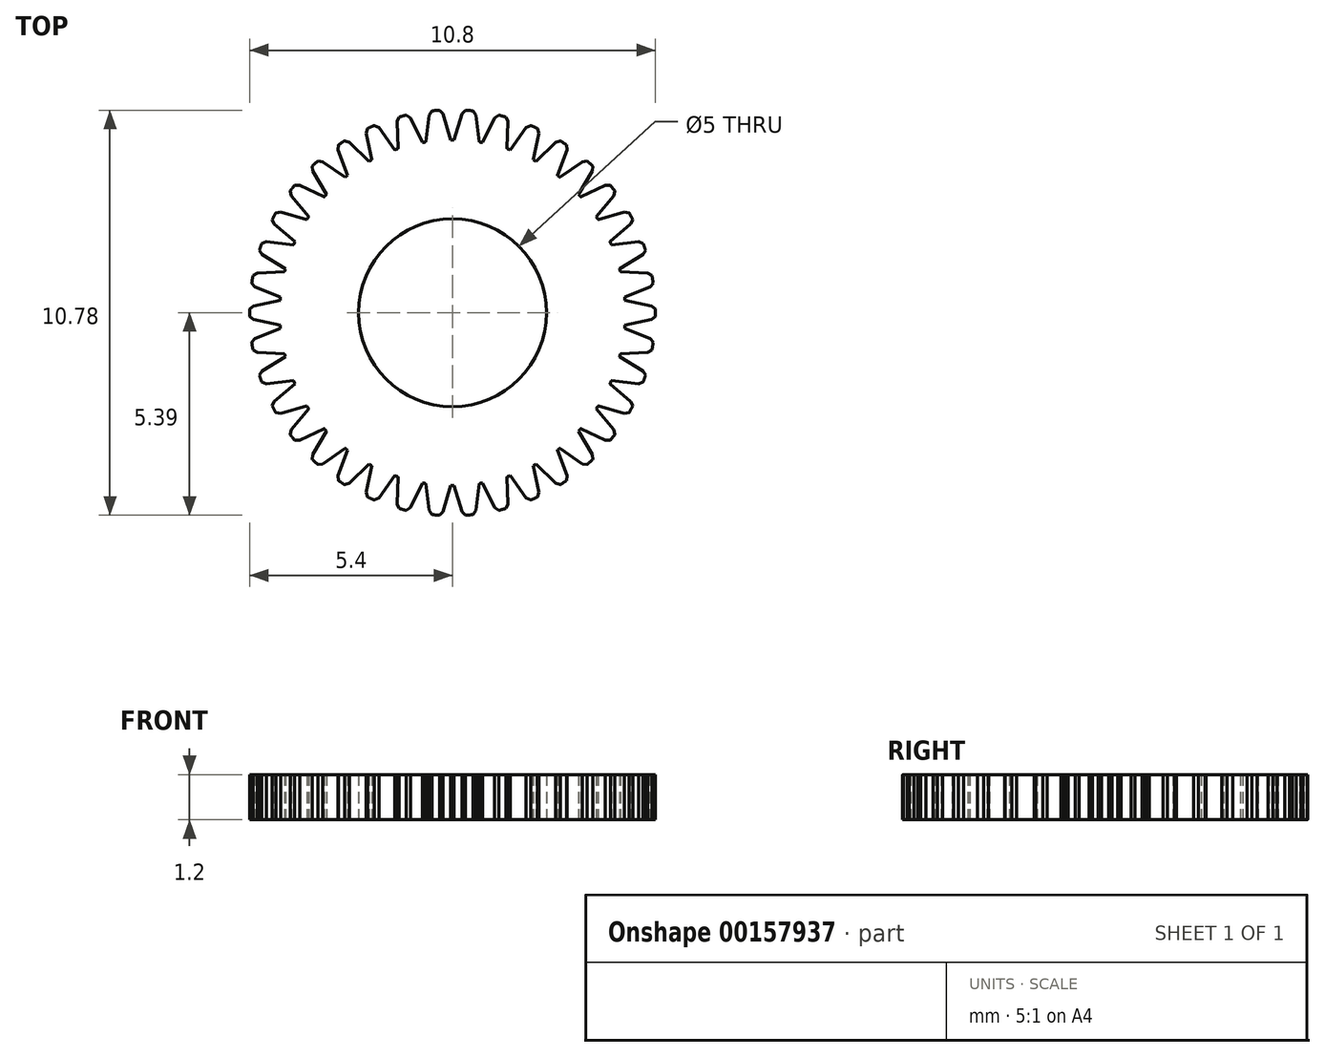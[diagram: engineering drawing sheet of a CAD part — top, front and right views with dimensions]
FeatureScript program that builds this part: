
annotation { "Feature Type Name" : "Feature", "Feature Type Description" : "" }
export const myFeature = defineFeature(function(context is Context, id is Id, definition is map)
    precondition{}
    {
        {
            assignVariable(context, id + "F0", {"name" : "D", "anyValue" : 1.08});
        }
        {
            assignVariable(context, id + "F1", {"name" : "n", "anyValue" : 38});
        }
        {
            assignVariable(context, id + "F2", {"name" : "h", "anyValue" : 1.2});
        }
        {
            var Q0;
            Q0=qCreatedBy(makeId("Front.planeOp"),FACE);
            var sketch = newSketch(context, id + "F3", { "sketchPlane" : qUnion([Q0])});
            skLineSegment(sketch, "E0", {"start": v(0, 0) * mm, "end": v(0, 36.61) * mm, "construction": true});
            skSolve(sketch);
        }
        {
            var Q0;
            Q0=qCreatedBy(makeId("Top.planeOp"),FACE);
            var sketch = newSketch(context, id + "F4", { "sketchPlane" : qUnion([Q0])});
            skCircle(sketch, "E1", {"center": v(0, 0) * mm, "radius": 5.4 * mm});
            skCircle(sketch, "E2", {"center": v(0, 0) * mm, "radius": 2.5 * mm});
            skCircle(sketch, "E3", {"center": v(0, 0) * mm, "radius": 4.6 * mm});
            skLineSegment(sketch, "E4", {"start": v(0, 0) * mm, "end": v(0, 5.4) * mm});
            skLineSegment(sketch, "E5", {"start": v(0, 0) * mm, "end": v(0.89, 5.33) * mm});
            skLineSegment(sketch, "E6", {"start": v(0, 0) * mm, "end": v(0.45, 5.38) * mm, "construction": true});
            skCircle(sketch, "E7", {"center": v(0, 0) * mm, "radius": 5 * mm, "construction": true});
            skLineSegment(sketch, "E8", {"start": v(0.28, 5.4) * mm, "end": v(0.04, 4.6) * mm});
            skLineSegment(sketch, "E9.MirrorCS", {"start": v(0.6, 5.37) * mm, "end": v(0.71, 4.54) * mm});
            skLineSegment(sketch, "E10", {"start": v(0.18, 5.4) * mm, "end": v(0, 0) * mm, "construction": true});
            skPoint(sketch, "E11", {"position": v(0.16, 5) * mm});
            skLineSegment(sketch, "E12", {"start": v(0.35, 5.39) * mm, "end": v(0.25, 5.3) * mm});
            skLineSegment(sketch, "E13.MirrorCS", {"start": v(0.54, 5.37) * mm, "end": v(0.62, 5.26) * mm});
            skSolve(sketch);
        }
        {
            var Q0;
            {var subQ6=sQuery(id+"F4.wireOp",EDGE,"E12");Q0=makeQuery(id+"F4.imprint","IMPRINT",FACE,{"disambiguationData":[TD([[makeQuery(id+"F4.imprint","IMPRINT",EDGE,{"derivedFrom":subQ6}),1.0]])]});}
            var Q1;
            {var subQ2=sQuery(id+"F4.wireOp",EDGE,"E4");var subQ7=sQuery(id+"F4.wireOp",EDGE,"E2");var subQ8=makeQuery(id+"F4.imprint","INTERSECT",VERTEX,{"derivedFrom":[subQ7,subQ2]});Q1=makeQuery(id+"F4.imprint","IMPRINT",FACE,{"disambiguationData":[TD([[makeQuery(id+"F4.imprint","IMPRINT",EDGE,{"disambiguationData":[TD([[subQ8,1.0]])],"derivedFrom":subQ7}),-1.0]])]});}
            extrude(context, id + "F5", {"entities" : qUnion([Q0, Q1]), "endBound" : BoundingType.SYMMETRIC, "depth" : (getVariable(context, 'h')) * mm});
        }
        {
            var Q0;
            Q0=makeQuery(id+"F5.opExtrude","SWEPT_BODY",BODY,{"disambiguationData":[OSD([sQuery(id+"F4.wireOp",EDGE,"E1"),sQuery(id+"F4.wireOp",EDGE,"E2"),sQuery(id+"F4.wireOp",EDGE,"E3"),sQuery(id+"F4.wireOp",EDGE,"E4"),sQuery(id+"F4.wireOp",EDGE,"E5"),sQuery(id+"F4.wireOp",EDGE,"E8"),sQuery(id+"F4.wireOp",EDGE,"E9.MirrorCS")])]});
            var Q1;
            Q1=sQuery(id+"F3.wireOp",EDGE,"E0");
            circularPattern(context, id + "F6", {"operationType" : NewBodyOperationType.ADD, "entities" : qUnion([Q0]), "axis" : qUnion([Q1]), "angle" : 360 * degree, "instanceCount" : getVariable(context, 'n'), "equalSpace" : true});
        }
        {
            var Q0;
            Q0=qCreatedBy(makeId("Front.planeOp"),FACE);
            cPlane(context, id + "F7", {"entities" : qUnion([Q0]), "cplaneType" : CPlaneType.OFFSET, "offset" : (getVariable(context, 'D') / 2) * mm, "width" : 150 * mm, "height" : 150 * mm});
        }
        {
            var Q0;
            Q0=qCreatedBy(id+"F7.planeOp",FACE);
            var sketch = newSketch(context, id + "F8", { "sketchPlane" : qUnion([Q0])});
            skLineSegment(sketch, "E14.bottom", {"start": v(5.4, 6) * mm, "end": v(-5.4, 6) * mm});
            skLineSegment(sketch, "E14.top", {"start": v(5.4, -6) * mm, "end": v(-5.4, -6) * mm});
            skLineSegment(sketch, "E14.left", {"start": v(5.4, 6) * mm, "end": v(5.4, -6) * mm});
            skLineSegment(sketch, "E14.right", {"start": v(-5.4, 6) * mm, "end": v(-5.4, -6) * mm});
            skPoint(sketch, "E14.middle", {"position": v(0, 0) * mm});
            skCircle(sketch, "E15", {"center": v(0, -4) * mm, "radius": 1.25 * mm});
            skSolve(sketch);
        }
        {
            var Q0;
            Q0=makeQuery(id+"F8.imprint","IMPRINT",FACE,{"disambiguationData":[TD([[makeQuery(id+"F8.imprint","IMPRINT",EDGE,{"derivedFrom":sQuery(id+"F8.wireOp",EDGE,"E15")}),1.0]])]});
            extrude(context, id + "F9", {"entities" : qUnion([Q0]), "operationType" : NewBodyOperationType.REMOVE, "oppositeDirection" : true, "depth" : (getVariable(context, 'D') / 2) * mm});
        }
    });
